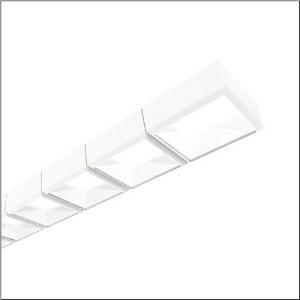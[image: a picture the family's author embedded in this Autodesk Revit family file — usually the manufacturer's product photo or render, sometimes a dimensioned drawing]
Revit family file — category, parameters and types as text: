
# Revit family: scriptus_r__11_5mz212d04wa_64be
name_source: partatom
category: Lighting Fixtures
units: mm (PartAtom-declared; Revit-internal decimal feet)

## family parameters
Cut with Voids When Loaded = No
Host = Face
Light Source = No
Part Type = Normal
Room Calculation Point = No
Round Connector Dimension = Use Diameter
Shared = No

## types (1)
- Scriptus® 11 (1 x LED 4000K / CRI = 80 (unbekannt), 2410 lm, 4000K)
    Apparent Load = 35 VA
    CIE Flux Codes = 82 95 99 100 100
    Color Rendering = 80
    Color Temperature = 4000K
    Default Elevation = 1800 mm
    Description = Scriptus® 11, office luminaire, primary optical cover: lenses, CAT 2 (L<= 3000cd/m²), light emission: direct distribution, primary light characteristic: symmetric, installation type: surface-mounted, LED, rated luminous flux: 4.810lm, luminous efficacy: 139lm/W, light colour: 840, colour temperature: 4000K, control gear: DALI, with terminal, 5-pole, mains connection: 230V, AC, 50Hz, rated input power: 35W, housing, luminaire housing, of aluminium, traffic white (RAL 9016), length: 1.658mm, width: 114mm, height: 57mm, protection rating (complete): IP20, insulation class (complete): insulation class I (protective earthing), certification: CE, ENEC, VDE, protection symbol: F, permissible operating ambient temperature: 0..+35°C, standard: EN 50419, packaging unit: 1 piece
    Height = 57 mm
    Lamp = 1 x LED 4000K / CRI >= 80 (unbekannt)
    Lamp Light Flux = 2410 lm
    Lamp count = 1
    Length = 1658 mm
    Luminous efficacy = 139 lm/W
    Manufacturer = Siteco
    ModVariant = No
    Model = 5MZ212D04WA
    Mounting Place = Ceiling
    Mounting Type = Surface mounted
    Number of Poles = 1
    OnlyDefault = Yes
    Power Factor = 1
    Product Name = Scriptus® 11
    Product group = office luminaire | ceiling mounted
    ProductGroupID = 302
    Protection Class = Protection class I
    Protection Degree = IP 20
    RLX_Detail_Level = 1
    RLX_Emergency_Light_Flux = 0 lm
    RLX_Emergency_Type = 0
    RLX_Emergency_Type_DB = No
    RlxData = <blob elided: 29465 chars, md5=ff0555eb>
    Socket = socket
    Standby Power = 0 W
    System Light Flux = 4820 lm
    System Power = 35 W
    Type Comments = Product without accessories
    Type Image = l_1004833.jpg
    URL = http://relux.com
    VarID = ---
    Voltage = 0 V
    Weight = 0.00 kg
    Width = 114 mm

## geometry (parser evidence)
native form markers: Blend x4, Sweep x13
no freeform markers — native parametric forms only
